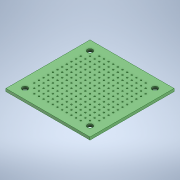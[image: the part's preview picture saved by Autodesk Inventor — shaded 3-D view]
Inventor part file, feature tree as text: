
AUTODESK INVENTOR PART (.ipt)
format: ipt  version: 2020.5 (Build 245400000, 400)  size: 390,656 bytes
history: native  units: mm
features: extrude x1, sketch x1
ambient origin geometry x8: Origin, YZ Plane, XZ Plane, XY Plane, X Axis, Y Axis, Z Axis, Center Point
bodies: Solid1 (feature_tree)
feature tree (2):
  extrude  "Extrusion1"  [1 undecoded]
  sketch  "Sketch1"  dims[d15=1.5mm d16=0.0mm]
note: 1 required parameter value undecoded (feature->parameter linkage not recoverable at this tier; creation-order binding heuristic only, values carry confidence <= 0.55)
